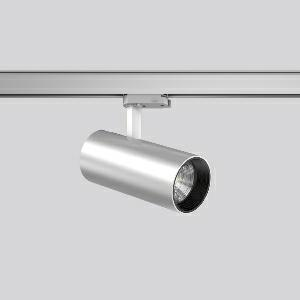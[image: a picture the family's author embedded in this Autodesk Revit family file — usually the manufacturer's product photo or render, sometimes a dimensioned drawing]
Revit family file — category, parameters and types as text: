
# Revit family: deecos_s_mini_742207_004_1_76_86e9
name_source: partatom
category: Lighting Fixtures
units: mm (PartAtom-declared; Revit-internal decimal feet)

## family parameters
Cut with Voids When Loaded = No
Host = Face
Light Source = No
Part Type = Normal
Room Calculation Point = No
Round Connector Dimension = Use Diameter
Shared = No

## types (1)
- DEECOS S mini (1 x LED Modul 940, 3200 lm, 4000)
    Apparent Load = 29 VA
    Approval mark = CE
    CIE Flux Codes = 96 100 100 100 100
    Color Rendering = 92
    Color Temperature = 4000
    Default Elevation = 1800 mm
    Description = Series: DEECOS S mini
LED surface-mounted projector in modern design with no visible cooling ribs. Housing: die-cast aluminium, powder-coated. Rotation range: 356°. Swivel range: 90°. Black plastic ring and recessed LED to prevent glare from the side. Optical assembly with lens made of plastic (polycarbonate) for the best homogeneous light distribution - can be changed without tools. Best colour rendering index Ra>90. With adapter for RZB 3-circuit DALI tracks. Suitable for Track on ceiling, Wall track. High quality converter without flickering and stroboscopic effect. The following accessories can be mounted without use of tools: interchangeable lenses, decorative glasses, honeycomb louvre, clear and frosted diffusers, white interchangeable plastic ring. 
Colour: silver
Diameter: 87 mm
Height: 214 mm
Lamp: LED
Socket: without socket
Colour temperature: 4000K
Colour rendering index (CRI): 92
System power: 29 W
Rated luminous flux: 3200 lm
Luminous efficiency: 110 lm/W
Control gear: Converter, dimmable, DALI
Protection class: I
Type of protection: IP 20
    Height = 214 mm
    Lamp = 1 x LED Modul 940
    Lamp Light Flux = 3200 lm
    Lamp count = 1
    Length = 87 mm
    Lifetime = 50000 h
    Luminous efficacy = 110 lm/W
    Manufacturer = RZB
    ModVariant = No
    Model = 742207.004.1.76
    Mounting Place = Ceiling
    Mounting Type = Rail mounted
    Number of Poles = 1
    OnlyDefault = Yes
    Power Factor = 1
    Product Name = DEECOS S mini
    Product group = Track mounted projectors
    ProductGroupID = 301
    Protection Class = Protection class I
    Protection Degree = IP 20
    RLX_Detail_Level = 1
    RLX_Emergency_Light_Flux = 0 lm
    RLX_Emergency_Type = 0
    RLX_Emergency_Type_DB = No
    RlxData = <blob elided: 37537 chars, md5=8825aa58>
    Socket = socket
    Standby Power = 0 W
    System Light Flux = 3200 lm
    System Power = 29 W
    Type Comments = Product without accessories
    Type Image = 741930.004.jpg
    URL = http://relux.com
    VarID = ---
    Voltage = 230 V
    Voltage Range = 220-240 V
    Weight = 0.00 kg
    Width = 0 mm  [stored 0 ft]

note: [stored X ft] marks values corroborated as IEEE doubles in the binary element streams (Revit-internal decimal feet)

## geometry (parser evidence)
native form markers: Blend x4, Sweep x11
no freeform markers — native parametric forms only
